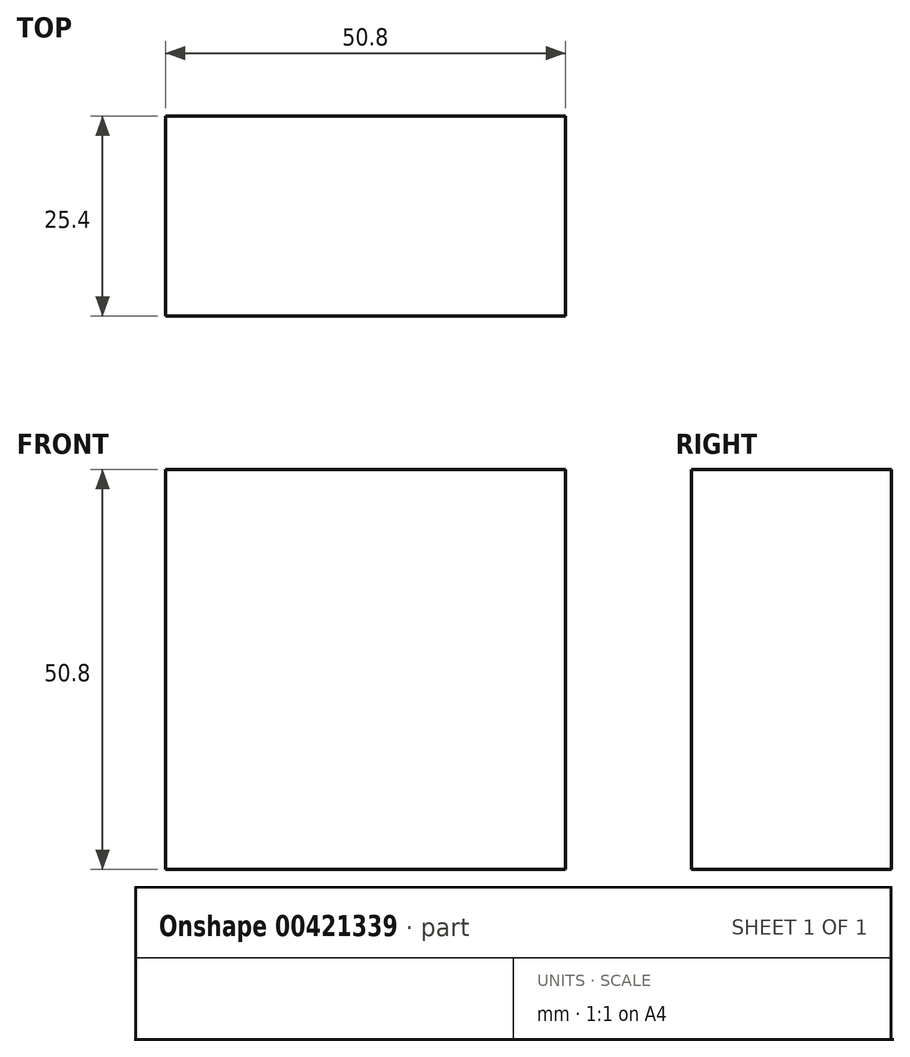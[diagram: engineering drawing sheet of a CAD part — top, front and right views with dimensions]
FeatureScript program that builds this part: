
annotation { "Feature Type Name" : "Feature", "Feature Type Description" : "" }
export const myFeature = defineFeature(function(context is Context, id is Id, definition is map)
    precondition{}
    {
        {
            var Q0;
            Q0=qCreatedBy(makeId("Top.planeOp"),FACE);
            var sketch = newSketch(context, id + "F0", { "sketchPlane" : qUnion([Q0])});
            skLineSegment(sketch, "E0", {"start": v(0, 0) * mm, "end": v(152.4, 0) * mm});
            skLineSegment(sketch, "E1", {"start": v(0, 0) * mm, "end": v(0, 76.2) * mm});
            skLineSegment(sketch, "E2", {"start": v(0, 76.2) * mm, "end": v(152.4, 76.2) * mm});
            skLineSegment(sketch, "E3", {"start": v(152.4, 76.2) * mm, "end": v(152.4, 0) * mm});
            skLineSegment(sketch, "E4", {"start": v(152.4, 0) * mm, "end": v(152.4, 25.4) * mm});
            skLineSegment(sketch, "E5", {"start": v(152.4, 25.4) * mm, "end": v(101.6, 25.4) * mm});
            skLineSegment(sketch, "E6", {"start": v(101.6, 25.4) * mm, "end": v(101.6, 0) * mm});
            skLineSegment(sketch, "E7", {"start": v(101.6, 0) * mm, "end": v(152.4, 0) * mm});
            skSolve(sketch);
        }
        {
            var Q0;
            Q0=makeQuery(id+"F0.imprint","IMPRINT",FACE,{"disambiguationData":[TD([[makeQuery(id+"F0.imprint","IMPRINT",EDGE,{"derivedFrom":sQuery(id+"F0.wireOp",EDGE,"E0")}),1.0]])]});
            extrude(context, id + "F1", {"entities" : qUnion([Q0]), "depth" : 50.8 * mm});
        }
        {
            var Q0;
            Q0=qCreatedBy(makeId("Top.planeOp"),FACE);
            var sketch = newSketch(context, id + "F2", { "sketchPlane" : qUnion([Q0])});
            skLineSegment(sketch, "E8", {"start": v(0, 0) * mm, "end": v(152.4, 0) * mm});
            skLineSegment(sketch, "E9", {"start": v(152.4, 0) * mm, "end": v(152.4, 25.4) * mm});
            skLineSegment(sketch, "E10", {"start": v(152.4, 25.4) * mm, "end": v(101.6, 25.4) * mm});
            skLineSegment(sketch, "E11", {"start": v(101.6, 25.4) * mm, "end": v(101.6, 0) * mm});
            skSolve(sketch);
        }
        {
            var Q0;
            {var subQ0=sQuery(id+"F2.wireOp",EDGE,"E9");Q0=makeQuery(id+"F2.imprint","IMPRINT",FACE,{"disambiguationData":[TD([[makeQuery(id+"F2.imprint","IMPRINT",EDGE,{"derivedFrom":subQ0}),1.0]])]});}
            extrude(context, id + "F3", {"entities" : qUnion([Q0]), "operationType" : NewBodyOperationType.ADD, "depth" : 25.4 * mm});
        }
    });
